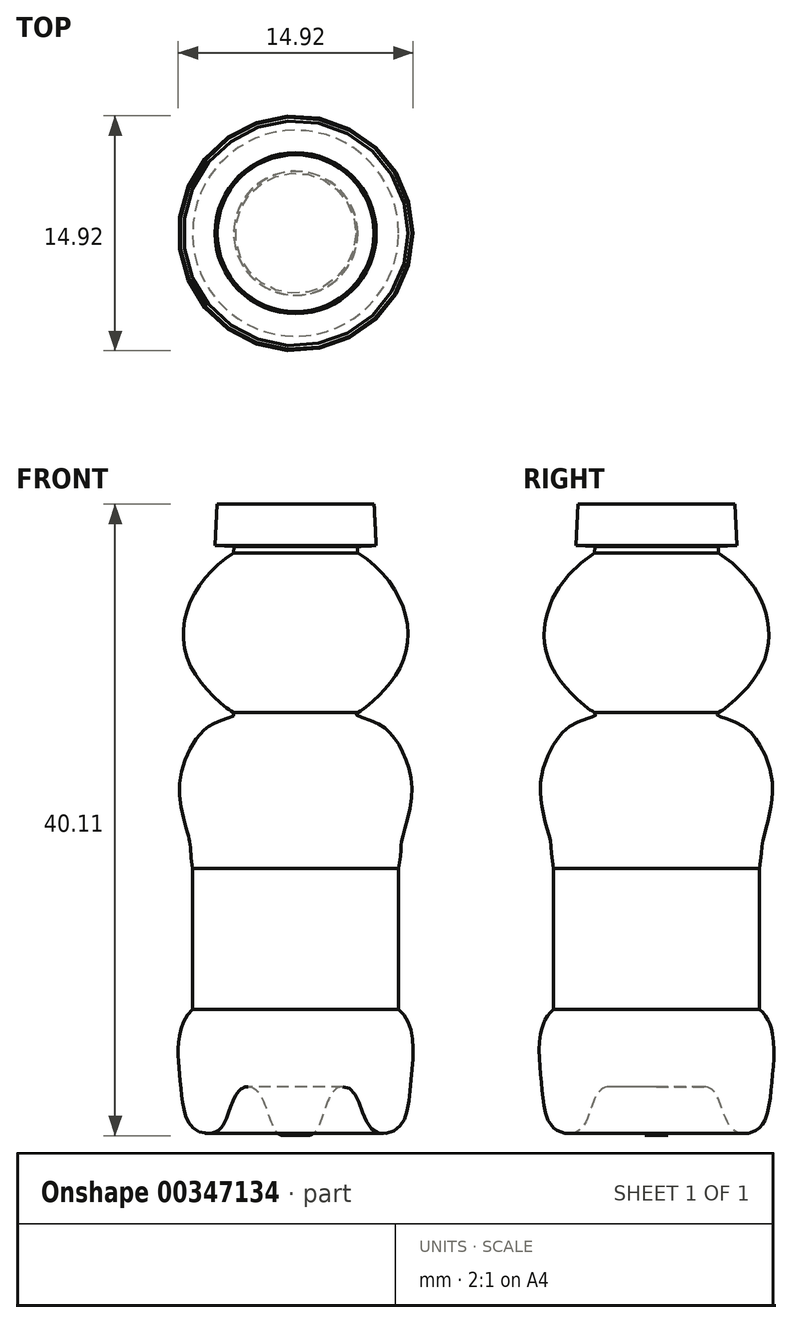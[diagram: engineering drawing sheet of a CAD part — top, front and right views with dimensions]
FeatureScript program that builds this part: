
annotation { "Feature Type Name" : "Feature", "Feature Type Description" : "" }
export const myFeature = defineFeature(function(context is Context, id is Id, definition is map)
    precondition{}
    {
        {
            var Q0;
            Q0=qCreatedBy(makeId("Front.planeOp"),FACE);
            var sketch = newSketch(context, id + "F0", { "sketchPlane" : qUnion([Q0])});
            skLineSegment(sketch, "E0", {"start": v(3.92, 44.4) * mm, "end": v(3.94, 43.98) * mm});
            skFitSpline(sketch, "E1", {"points": [v(3.94, 43.98) * mm, v(6.88, 37.27) * mm, v(3.94, 33.86) * mm], "startDerivative": vector(13.72, -8.32) * mm, "endDerivative": vector(-2.69, -1.37) * mm});
            skLineSegment(sketch, "E2", {"start": v(3.92, 44.4) * mm, "end": v(5.11, 44.46) * mm});
            skLineSegment(sketch, "E3", {"start": v(5.11, 44.46) * mm, "end": v(4.98, 47.1) * mm});
            skLineSegment(sketch, "E4", {"start": v(4.98, 47.1) * mm, "end": v(0, 47.1) * mm});
            skFitSpline(sketch, "E5", {"points": [v(3.94, 33.86) * mm, v(4.9, 33.29) * mm, v(6.5, 31.9) * mm, v(7.38, 28.87) * mm, v(6.73, 25.67) * mm, v(6.54, 23.97) * mm], "startDerivative": vector(-9, -3.68) * mm, "endDerivative": vector(-3.52, -22) * mm});
            skLineSegment(sketch, "E6", {"start": v(6.54, 23.97) * mm, "end": v(6.54, 15) * mm});
            skFitSpline(sketch, "E7", {"points": [v(6.54, 15) * mm, v(7.4, 13.2) * mm, v(7.27, 9.9) * mm, v(6.54, 7.5) * mm, v(4.86, 7.36) * mm, v(3.65, 9.77) * mm, v(2.45, 9.84) * mm, v(1.17, 7.16) * mm, v(0, 7.16) * mm], "startDerivative": vector(12.15, -10.08) * mm, "endDerivative": vector(-13.87, 4.87) * mm});
            skLineSegment(sketch, "E8", {"start": v(0, 49.46) * mm, "end": v(0, 4.61) * mm});
            skSolve(sketch);
        }
        {
            var Q0;
            Q0 = qSketchRegion(id + "F0", true);
            var Q1;
            Q1=sQuery(id+"F0.wireOp",EDGE,"E8");
            revolve(context, id + "F1", {"entities" : qUnion([Q0]), "axis" : qUnion([Q1]), "revolveType" : RevolveType.FULL});
        }
    });
